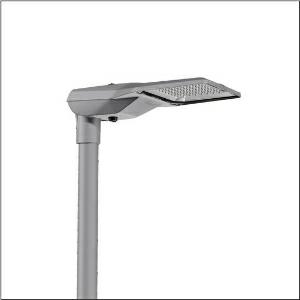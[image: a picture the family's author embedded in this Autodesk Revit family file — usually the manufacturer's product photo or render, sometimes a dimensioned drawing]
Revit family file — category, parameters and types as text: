
# Revit family: streetlight_sl_21_midi___st0_5a_5xe3b43t08lb_fa0c
name_source: partatom
category: Lighting Fixtures
units: mm (PartAtom-declared; Revit-internal decimal feet)

## family parameters
Cut with Voids When Loaded = No
Host = Face
Light Source = No
Part Type = Normal
Room Calculation Point = No
Round Connector Dimension = Use Diameter
Shared = No

## types (1)
- --- (1 x LED, 14950 lm, 99.6 W, 4000K)
    Apparent Load = 100 VA
    CIE Flux Codes = 41 75 97 100 100
    Color Rendering = 70
    Color Temperature = 4000K
    Default Elevation = 1800 mm
    Description = Streetlight SL 21 midi, mast luminaire, primary light control with lens, of PMMA, primary optical cover: cover, of toughened safety glass, transparent, light distribution: ST0.5a, light emission: direct distribution, primary light characteristic: asymmetric, installation type: side-entry, post-top, LED, High Power LED, rated luminous flux: 14.950lm, luminous efficacy: 150lm/W, light colour: 740, colour temperature: 4000K, control gear: D4i, control: overheat protection, constant luminous flux control, time-dependent luminous flux control, flexible luminous flux parameterisation, pre-setting: logarithmic dimming characteristic, mains connection: 230..240V, AC, 50/60Hz, start of lifetime: 100W, end of service life: 102W, reduction: 46W, luminaire housing, of diecast aluminium, powder-coated, Siteco® metallic grey (DB 702S), corrosivity category C5 mid according to DIN EN ISO 12944, please order mast flange separately, inclination adjustable: 0°, 5°, 10°, 15°, sealing non-destructively replaceable, multi-level sealing system, length: 644mm, width: 335mm, height: 110mm, mast flange for spigot size: 42mm (side-entry): 5XC10008XM4, 60/48mm (side-entry/post-top): 5XC10108XM2, 76/60mm (side-entry/post-top): 5XC10108XM1, mounting height: 4..8m, Smart Interface below and above, protection rating (complete): IP66, insulation class (complete): insulation class II (safety insulation), certification: CE, ENEC, ENEC+, VDE, impact resistance: IK10, permissible operating ambient temperature for outdoor applications: -40..+50°C, standard-compliant lighting for roads and squares, packaging unit: 1 piece

Light Distribution: ST0.5a
    Height = 111 mm
    Lamp = 1 x LED
    Lamp Light Flux = 14950 lm
    Lamp Power = 99.6 W
    Lamp count = 1
    Length = 644 mm
    Luminous efficacy = 150 lm/W
    Manufacturer = Siteco
    ModVariant = No
    Model = 5XE3B43T08LB
    Number of Poles = 1
    OnlyDefault = Yes
    Power Factor = 1
    Product Name = Streetlight SL 21 midi | ST0.5a
    Product group = mast luminaire | pylon top
    ProductGroupID = 6100
    Protection Class = Protection class II
    Protection Degree = IP 66
    RLX_Detail_Level = 1
    RLX_Emergency_Light_Flux = 0 lm
    RLX_Emergency_Type = 0
    RLX_Emergency_Type_DB = No
    RlxData = <blob elided: 37953 chars, md5=1e2e0b56>
    Socket = socket
    Standby Power = 0 W
    System Light Flux = 14950 lm
    System Power = 100 W
    Type Comments = factory setting: luminous flux: 100 % | dim-lin: 254 | 1020 mA
    Type Image = l_1004304.jpg
    URL = http://relux.com
    VarID = @adj_032541
    Voltage = 0 V
    Weight = 0.00 kg
    Width = 336 mm

## geometry (parser evidence)
native form markers: Blend x4, Sweep x12
no freeform markers — native parametric forms only
